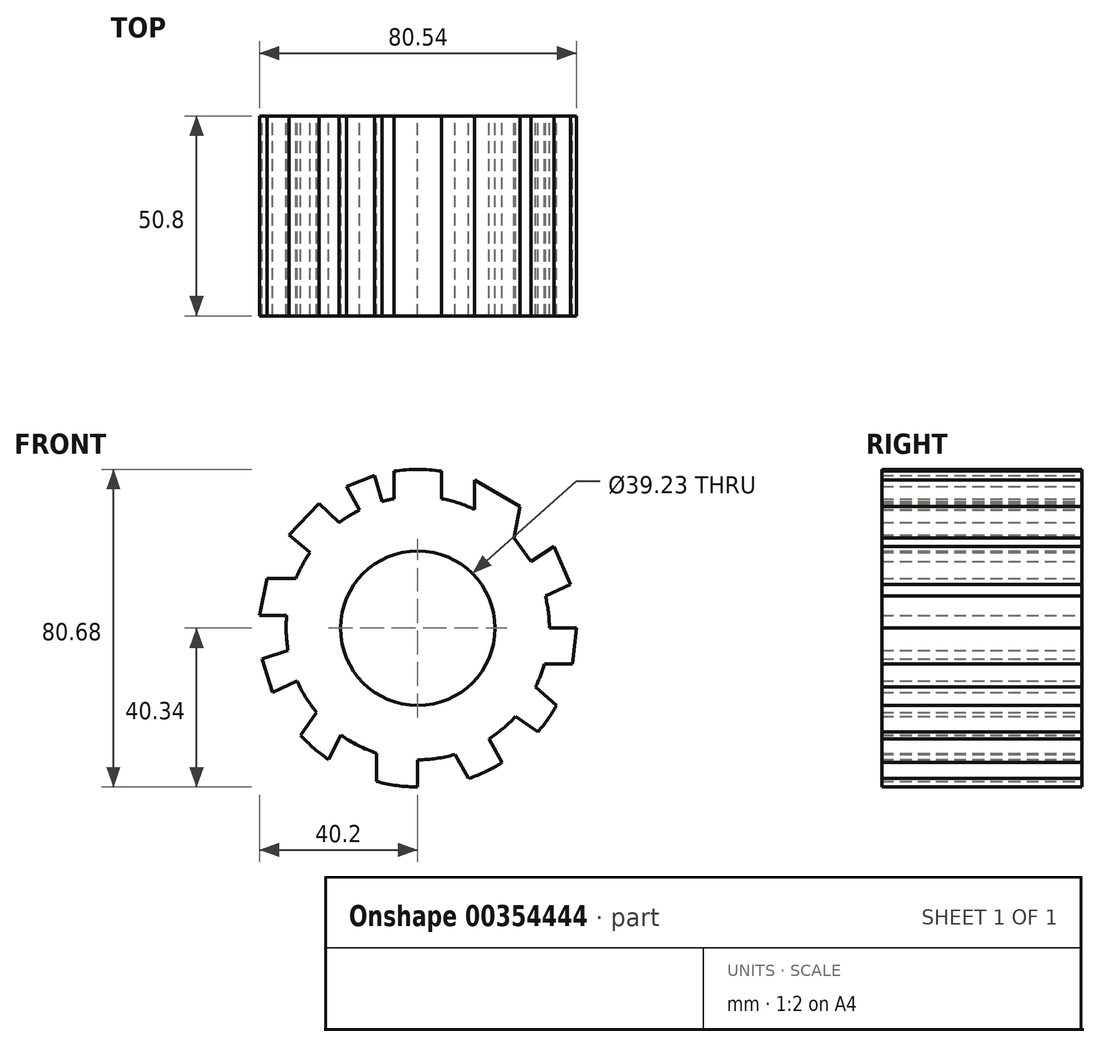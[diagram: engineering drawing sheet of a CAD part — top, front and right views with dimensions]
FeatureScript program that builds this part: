
annotation { "Feature Type Name" : "Feature", "Feature Type Description" : "" }
export const myFeature = defineFeature(function(context is Context, id is Id, definition is map)
    precondition{}
    {
        {
            var Q0;
            Q0=qCreatedBy(makeId("Front.planeOp"),FACE);
            var sketch = newSketch(context, id + "F0", { "sketchPlane" : qUnion([Q0])});
            skArc(sketch, "E0", {"start": v(-6.05, 32.88) * mm, "mid": v(-7.55, 32.57) * mm, "end": v(-9.03, 32.2) * mm});
            skCircle(sketch, "E1", {"center": v(0, 0) * mm, "radius": 19.62 * mm});
            skArc(sketch, "E2", {"start": v(39.3, -9.1) * mm, "mid": v(40.07, -4.58) * mm, "end": v(40.34, 0) * mm});
            skLineSegment(sketch, "E3", {"start": v(-6.05, 39.88) * mm, "end": v(-6.05, 32.88) * mm});
            skLineSegment(sketch, "E4", {"start": v(6.05, 32.88) * mm, "end": v(6.05, 39.88) * mm});
            skLineSegment(sketch, "E5", {"start": v(14.42, 30.17) * mm, "end": v(14.42, 37.67) * mm});
            skLineSegment(sketch, "E6", {"start": v(14.42, 37.67) * mm, "end": v(25.95, 30.88) * mm});
            skLineSegment(sketch, "E7", {"start": v(25.95, 30.88) * mm, "end": v(24.4, 22.86) * mm});
            skLineSegment(sketch, "E8", {"start": v(24.4, 22.86) * mm, "end": v(28.82, 16.96) * mm});
            skLineSegment(sketch, "E9", {"start": v(28.82, 16.96) * mm, "end": v(34.56, 20.8) * mm});
            skLineSegment(sketch, "E10", {"start": v(34.56, 20.8) * mm, "end": v(38.77, 11.14) * mm});
            skLineSegment(sketch, "E11", {"start": v(38.77, 11.14) * mm, "end": v(32.4, 8.24) * mm});
            skLineSegment(sketch, "E12", {"start": v(33.44, 0) * mm, "end": v(40.34, 0) * mm});
            skLineSegment(sketch, "E13", {"start": v(40.34, 0) * mm, "end": v(39.3, -9.1) * mm});
            skLineSegment(sketch, "E14", {"start": v(39.3, -9.1) * mm, "end": v(32.18, -9.1) * mm});
            skLineSegment(sketch, "E15", {"start": v(29.9, -14.98) * mm, "end": v(35.27, -19.57) * mm});
            skLineSegment(sketch, "E16", {"start": v(30.58, -26.3) * mm, "end": v(24.78, -22.45) * mm});
            skArc(sketch, "E17.trimOffspring", {"start": v(38.77, 11.14) * mm, "mid": v(36.98, 16.1) * mm, "end": v(34.56, 20.8) * mm});
            skArc(sketch, "E18.trimOffspring", {"start": v(25.95, 30.88) * mm, "mid": v(20.47, 34.76) * mm, "end": v(14.42, 37.67) * mm});
            skArc(sketch, "E19.trimOffspring", {"start": v(6.05, 39.88) * mm, "mid": v(0, 40.34) * mm, "end": v(-6.05, 39.88) * mm});
            skPoint(sketch, "E20.orphan", {"position": v(0, 33.44) * mm});
            skArc(sketch, "E21.trimOffspring", {"start": v(14.42, 30.17) * mm, "mid": v(10.33, 31.8) * mm, "end": v(6.05, 32.88) * mm});
            skArc(sketch, "E22.trimOffspring", {"start": v(28.82, 16.96) * mm, "mid": v(26.77, 20.03) * mm, "end": v(24.4, 22.86) * mm});
            skArc(sketch, "E23.trimOffspring", {"start": v(33.44, 0) * mm, "mid": v(33.18, 4.15) * mm, "end": v(32.4, 8.24) * mm});
            skArc(sketch, "E24.trimOffspring", {"start": v(29.9, -14.98) * mm, "mid": v(31.17, -12.1) * mm, "end": v(32.18, -9.1) * mm});
            skLineSegment(sketch, "E25", {"start": v(18.05, -28.14) * mm, "end": v(21.45, -34.16) * mm});
            skLineSegment(sketch, "E26", {"start": v(12.95, -38.2) * mm, "end": v(9.4, -32.09) * mm});
            skArc(sketch, "E27.trimOffspring", {"start": v(18.05, -28.14) * mm, "mid": v(21.6, -25.52) * mm, "end": v(24.78, -22.45) * mm});
            skArc(sketch, "E28.trimOffspring", {"start": v(30.58, -26.3) * mm, "mid": v(33.1, -23.05) * mm, "end": v(35.27, -19.57) * mm});
            skLineSegment(sketch, "E29", {"start": v(0, -33.44) * mm, "end": v(0, -40.34) * mm});
            skLineSegment(sketch, "E30", {"start": v(-10.46, -38.95) * mm, "end": v(-10.46, -31.76) * mm});
            skArc(sketch, "E31.trimOffspring", {"start": v(12.95, -38.2) * mm, "mid": v(17.32, -36.43) * mm, "end": v(21.45, -34.16) * mm});
            skArc(sketch, "E32.trimOffspring", {"start": v(0, -33.44) * mm, "mid": v(4.75, -33.1) * mm, "end": v(9.4, -32.09) * mm});
            skLineSegment(sketch, "E33", {"start": v(-19.53, -27.14) * mm, "end": v(-22.63, -33.39) * mm});
            skLineSegment(sketch, "E34", {"start": v(-29.74, -27.25) * mm, "end": v(-25.72, -21.36) * mm});
            skArc(sketch, "E35.trimOffspring", {"start": v(-10.46, -38.95) * mm, "mid": v(-5.28, -39.99) * mm, "end": v(0, -40.34) * mm});
            skArc(sketch, "E36.trimOffspring", {"start": v(-19.53, -27.14) * mm, "mid": v(-15.17, -29.8) * mm, "end": v(-10.46, -31.76) * mm});
            skLineSegment(sketch, "E37", {"start": v(-30.63, -13.41) * mm, "end": v(-36.86, -16.39) * mm});
            skLineSegment(sketch, "E38", {"start": v(-36.86, -16.39) * mm, "end": v(-39.57, -7.8) * mm});
            skLineSegment(sketch, "E39", {"start": v(-39.57, -7.8) * mm, "end": v(-32.95, -5.7) * mm});
            skArc(sketch, "E40.trimOffspring", {"start": v(-29.74, -27.25) * mm, "mid": v(-26.37, -30.52) * mm, "end": v(-22.63, -33.39) * mm});
            skArc(sketch, "E41.trimOffspring", {"start": v(-30.63, -13.41) * mm, "mid": v(-28.46, -17.56) * mm, "end": v(-25.72, -21.36) * mm});
            skLineSegment(sketch, "E42", {"start": v(-33.28, 3.26) * mm, "end": v(-40.2, 3.26) * mm});
            skLineSegment(sketch, "E43", {"start": v(-40.2, 3.26) * mm, "end": v(-38.3, 12.66) * mm});
            skLineSegment(sketch, "E44", {"start": v(-38.3, 12.66) * mm, "end": v(-30.95, 12.66) * mm});
            skArc(sketch, "E45.trimOffspring", {"start": v(-39.57, -7.8) * mm, "mid": v(-38.46, -12.17) * mm, "end": v(-36.86, -16.39) * mm});
            skArc(sketch, "E46.trimOffspring", {"start": v(-33.28, 3.26) * mm, "mid": v(-33.41, -1.24) * mm, "end": v(-32.95, -5.7) * mm});
            skLineSegment(sketch, "E47", {"start": v(-27.35, 19.24) * mm, "end": v(-32.7, 23.63) * mm});
            skLineSegment(sketch, "E48", {"start": v(-32.7, 23.63) * mm, "end": v(-25.04, 31.62) * mm});
            skLineSegment(sketch, "E49", {"start": v(-25.04, 31.62) * mm, "end": v(-20, 26.8) * mm});
            skLineSegment(sketch, "E50", {"start": v(-14.74, 30.01) * mm, "end": v(-18.08, 36.06) * mm});
            skLineSegment(sketch, "E51", {"start": v(-18.08, 36.06) * mm, "end": v(-11, 38.8) * mm});
            skLineSegment(sketch, "E52", {"start": v(-11, 38.8) * mm, "end": v(-9.03, 32.2) * mm});
            skArc(sketch, "E53.trimOffspring", {"start": v(-38.3, 12.66) * mm, "mid": v(-39.53, 8.01) * mm, "end": v(-40.2, 3.26) * mm});
            skArc(sketch, "E54.trimOffspring", {"start": v(-25.04, 31.62) * mm, "mid": v(-29.14, 27.89) * mm, "end": v(-32.7, 23.63) * mm});
            skArc(sketch, "E55.trimOffspring", {"start": v(-11, 38.8) * mm, "mid": v(-14.6, 37.6) * mm, "end": v(-18.08, 36.06) * mm});
            skArc(sketch, "E56.trimOffspring", {"start": v(-14.74, 30.01) * mm, "mid": v(-17.44, 28.53) * mm, "end": v(-20, 26.8) * mm});
            skArc(sketch, "E57.trimOffspring", {"start": v(-27.35, 19.24) * mm, "mid": v(-29.33, 16.05) * mm, "end": v(-30.95, 12.66) * mm});
            skSolve(sketch);
        }
        {
            var Q0;
            Q0=makeQuery(id+"F0.imprint","IMPRINT",FACE,{"disambiguationData":[TD([[makeQuery(id+"F0.imprint","IMPRINT",EDGE,{"derivedFrom":sQuery(id+"F0.wireOp",EDGE,"E0")}),1.0]])]});
            extrude(context, id + "F1", {"entities" : qUnion([Q0]), "depth" : 50.8 * mm});
        }
    });
